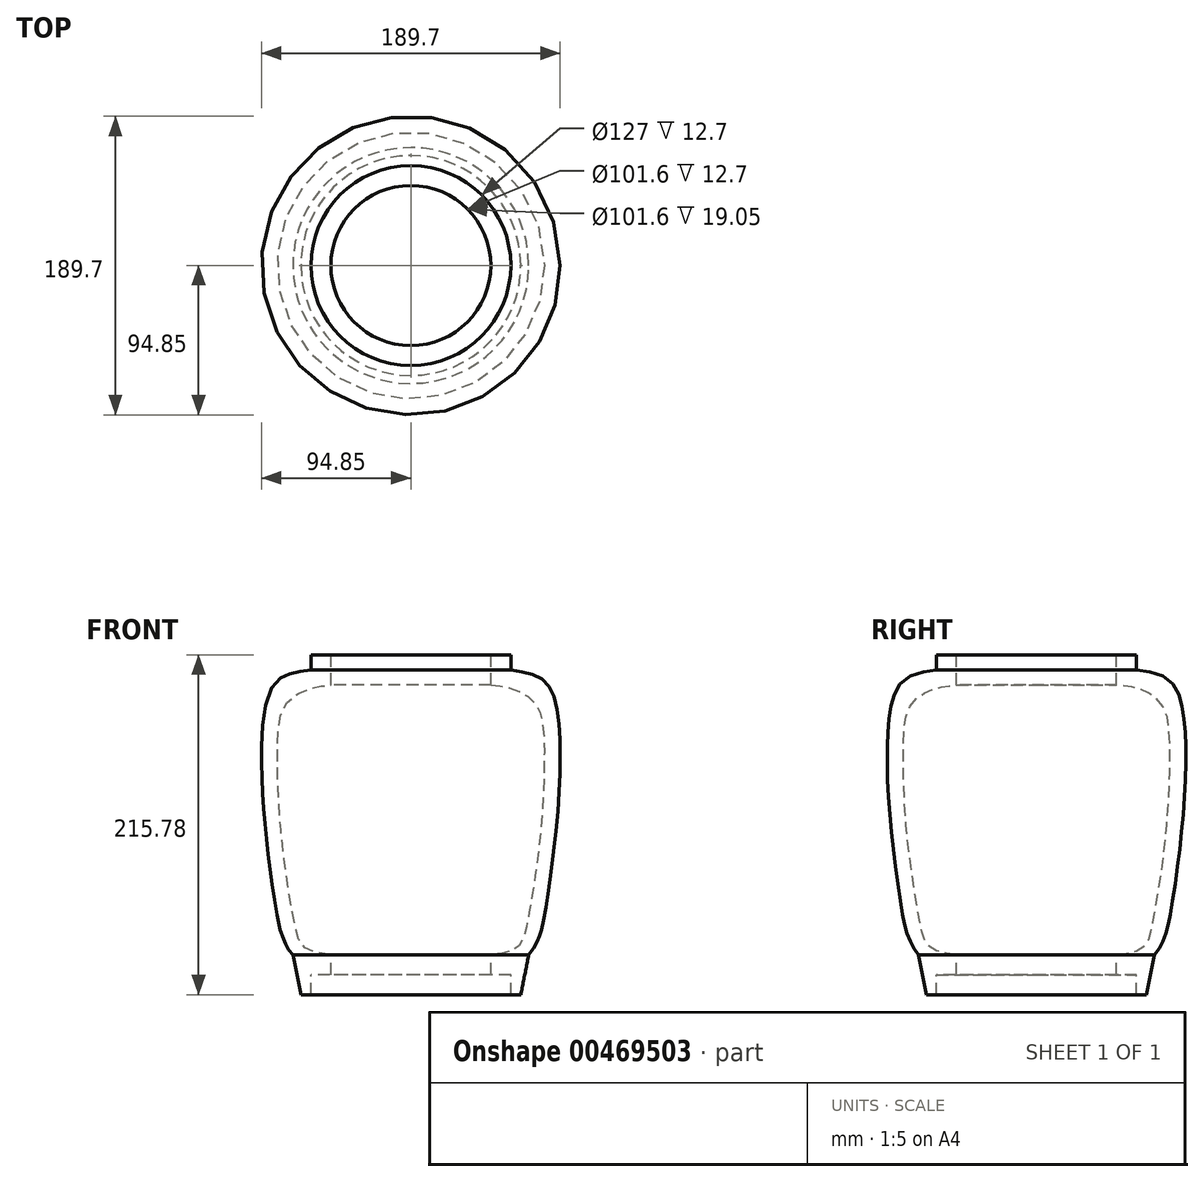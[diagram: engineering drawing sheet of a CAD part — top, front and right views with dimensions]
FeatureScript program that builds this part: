
annotation { "Feature Type Name" : "Feature", "Feature Type Description" : "" }
export const myFeature = defineFeature(function(context is Context, id is Id, definition is map)
    precondition{}
    {
        {
            var Q0;
            Q0=qCreatedBy(makeId("Front.planeOp"),FACE);
            var sketch = newSketch(context, id + "F0", { "sketchPlane" : qUnion([Q0])});
            skLineSegment(sketch, "E0", {"start": v(-50.8, 12.7) * mm, "end": v(-63.5, 12.7) * mm});
            skLineSegment(sketch, "E1", {"start": v(-63.5, 12.7) * mm, "end": v(-63.5, 0) * mm});
            skLineSegment(sketch, "E2", {"start": v(-63.5, 0) * mm, "end": v(-69.85, 0) * mm});
            skLineSegment(sketch, "E3", {"start": v(-69.85, 0) * mm, "end": v(-74.9, 25.3) * mm});
            skLineSegment(sketch, "E4", {"start": v(-50.8, 215.78) * mm, "end": v(-63.5, 215.78) * mm});
            skLineSegment(sketch, "E5", {"start": v(-63.5, 215.78) * mm, "end": v(-63.5, 206.13) * mm});
            skFitSpline(sketch, "E6", {"points": [v(-63.5, 206.13) * mm, v(-85.04, 199.2) * mm, v(-94.23, 169.15) * mm, v(-92.22, 104.17) * mm, v(-83.6, 44.06) * mm, v(-80.78, 35.23) * mm, v(-74.9, 25.3) * mm], "startDerivative": vector(-163.93, -21.92) * mm, "endDerivative": vector(82.33, -81.74) * mm});
            skLineSegment(sketch, "E7", {"start": v(-50.8, 215.78) * mm, "end": v(-50.8, 196.73) * mm});
            skLineSegment(sketch, "E8", {"start": v(-50.8, 12.7) * mm, "end": v(-50.8, 25.4) * mm});
            skFitSpline(sketch, "E9", {"points": [v(-50.8, 196.73) * mm, v(-65.55, 194.02) * mm, v(-79.36, 184.54) * mm, v(-84.44, 164.15) * mm, v(-82.4, 103.56) * mm, v(-73.67, 44.4) * mm, v(-67.38, 29.75) * mm, v(-50.8, 25.4) * mm], "startDerivative": vector(-131.5, -14.73) * mm, "endDerivative": vector(168.7, -19.08) * mm});
            skLineSegment(sketch, "E10", {"start": v(0, 215.56) * mm, "end": v(0, 0) * mm, "construction": true});
            skPoint(sketch, "E11", {"position": v(-84.44, 169.15) * mm});
            skSolve(sketch);
        }
        {
            var Q0;
            Q0=makeQuery(id+"F0.imprint","IMPRINT",FACE,{"disambiguationData":[TD([[makeQuery(id+"F0.imprint","IMPRINT",EDGE,{"derivedFrom":sQuery(id+"F0.wireOp",EDGE,"E0")}),-1.0]])]});
            var Q1;
            Q1=sQuery(id+"F0.wireOp",EDGE,"E10");
            revolve(context, id + "F1", {"entities" : qUnion([Q0]), "axis" : qUnion([Q1]), "revolveType" : RevolveType.FULL});
        }
    });
